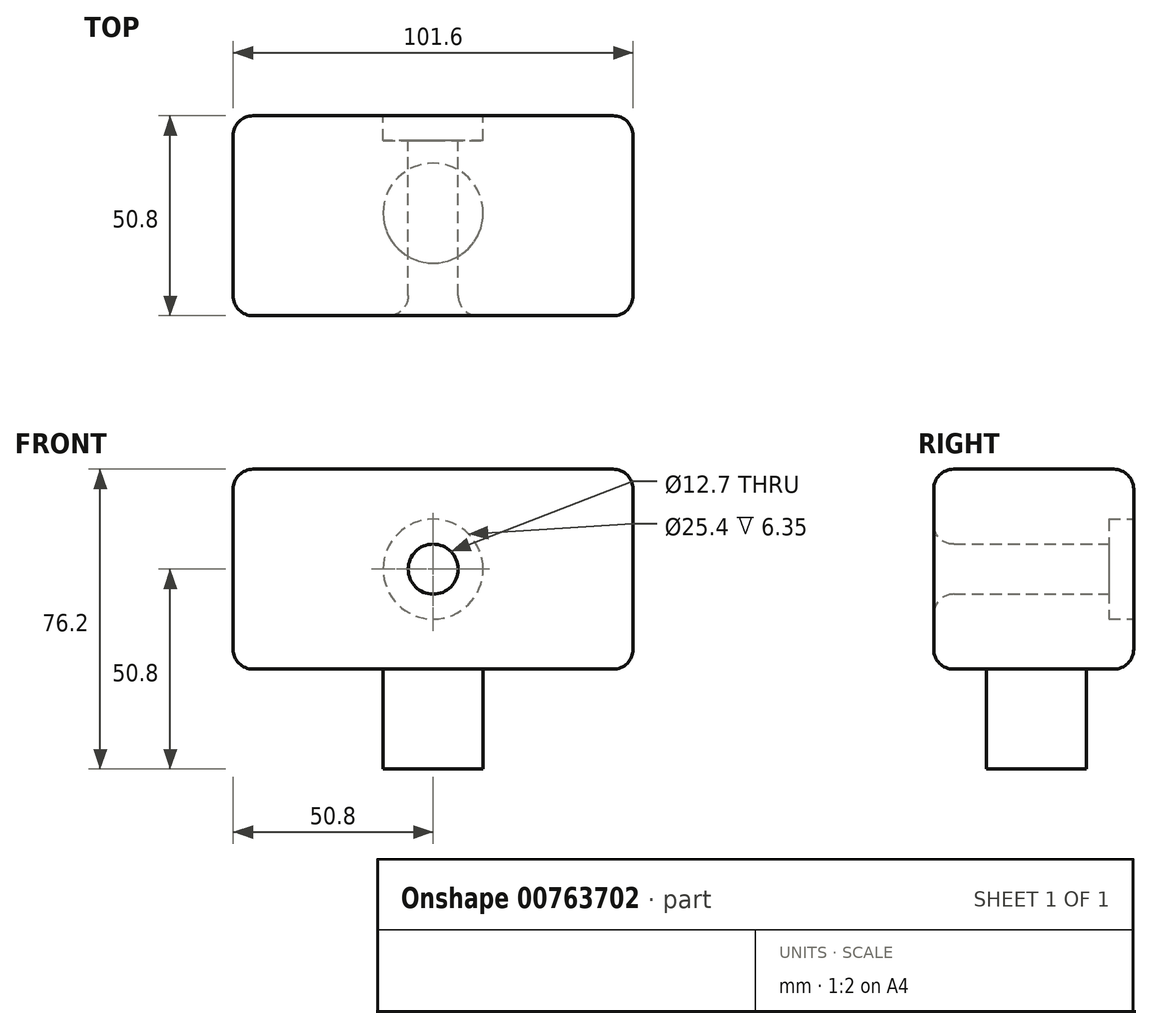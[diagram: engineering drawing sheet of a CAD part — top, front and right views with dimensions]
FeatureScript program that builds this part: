
annotation { "Feature Type Name" : "Feature", "Feature Type Description" : "" }
export const myFeature = defineFeature(function(context is Context, id is Id, definition is map)
    precondition{}
    {
        {
            var Q0;
            Q0=qCreatedBy(makeId("Top.planeOp"),FACE);
            var sketch = newSketch(context, id + "F0", { "sketchPlane" : qUnion([Q0])});
            skLineSegment(sketch, "E0.bottom", {"start": v(0, 0) * mm, "end": v(101.6, 0) * mm});
            skLineSegment(sketch, "E0.top", {"start": v(0, 50.8) * mm, "end": v(101.6, 50.8) * mm});
            skLineSegment(sketch, "E0.left", {"start": v(0, 0) * mm, "end": v(0, 50.8) * mm});
            skLineSegment(sketch, "E0.right", {"start": v(101.6, 0) * mm, "end": v(101.6, 50.8) * mm});
            skSolve(sketch);
        }
        {
            var Q0;
            Q0=makeQuery(id+"F0.imprint","IMPRINT",FACE,{"disambiguationData":[TD([[makeQuery(id+"F0.imprint","IMPRINT",EDGE,{"derivedFrom":sQuery(id+"F0.wireOp",EDGE,"E0.bottom")}),1.0]])]});
            extrude(context, id + "F1", {"entities" : qUnion([Q0]), "depth" : 50.8 * mm, "offsetDistance" : 25.4 * mm});
        }
        {
            var Q0;
            Q0=makeQuery(id+"F1.opExtrude","SWEPT_FACE",FACE,{"disambiguationData":[OSD([sQuery(id+"F0.wireOp",EDGE,"E0.top")])]});
            var sketch = newSketch(context, id + "F2", { "sketchPlane" : qUnion([Q0])});
            skPoint(sketch, "E1", {"position": v(-50.8, 25.4) * mm});
            skSolve(sketch);
        }
        {
            var Q0;
            Q0=sQuery(id+"F2.wireOp",VERTEX,"E1");
            var Q1;
            Q1=makeQuery(id+"F1.opExtrude","SWEPT_BODY",BODY,{"disambiguationData":[OSD([sQuery(id+"F0.wireOp",EDGE,"E0.bottom"),sQuery(id+"F0.wireOp",EDGE,"E0.top"),sQuery(id+"F0.wireOp",EDGE,"E0.left"),sQuery(id+"F0.wireOp",EDGE,"E0.right")])]});
            hole(context, id + "F3", {"style" : HoleStyle.C_BORE, "endStyle" : HoleEndStyle.THROUGH, "holeDiameter" : 12.7 * mm, "cBoreDiameter" : 25.4 * mm, "cBoreDepth" : 6.35 * mm, "majorDiameter" : 6.35 * mm, "isTappedThrough" : true, "tappedDepth" : 12.7 * mm, "tapClearance" : 3, "locations" : qUnion([Q0]), "scope" : qUnion([Q1])});
        }
        {
            var Q0;
            Q0=makeQuery(id+"F1.opExtrude","CAP_FACE",FACE,{"disambiguationData":[OSD([sQuery(id+"F0.wireOp",EDGE,"E0.bottom"),sQuery(id+"F0.wireOp",EDGE,"E0.top"),sQuery(id+"F0.wireOp",EDGE,"E0.left"),sQuery(id+"F0.wireOp",EDGE,"E0.right")])],"isStart":true});
            cPlane(context, id + "F4", {"entities" : qUnion([Q0]), "cplaneType" : CPlaneType.OFFSET, "offset" : 25.4 * mm, "width" : 152.4 * mm, "height" : 152.4 * mm});
        }
        {
            var Q0;
            Q0=qCreatedBy(id+"F4.planeOp",FACE);
            var sketch = newSketch(context, id + "F5", { "sketchPlane" : qUnion([Q0])});
            skCircle(sketch, "E2", {"center": v(50.8, -26.06) * mm, "radius": 12.7 * mm});
            skSolve(sketch);
        }
        {
            var Q0;
            Q0=makeQuery(id+"F5.imprint","IMPRINT",FACE,{"disambiguationData":[TD([[makeQuery(id+"F5.imprint","IMPRINT",EDGE,{"derivedFrom":sQuery(id+"F5.wireOp",EDGE,"E2")}),1.0]])]});
            extrude(context, id + "F6", {"entities" : qUnion([Q0]), "endBound" : BoundingType.UP_TO_NEXT, "oppositeDirection" : true, "depth" : 25.4 * mm, "offsetDistance" : 25.4 * mm});
        }
        {
            var Q0;
            Q0=makeQuery(id+"F1.opExtrude","SWEPT_FACE",FACE,{"disambiguationData":[OSD([sQuery(id+"F0.wireOp",EDGE,"E0.right")])]});
            var Q1;
            Q1=makeQuery(id+"F1.opExtrude","SWEPT_FACE",FACE,{"disambiguationData":[OSD([sQuery(id+"F0.wireOp",EDGE,"E0.left")])]});
            var Q2;
            Q2=makeQuery(id+"F1.opExtrude","CAP_FACE",FACE,{"disambiguationData":[OSD([sQuery(id+"F0.wireOp",EDGE,"E0.bottom"),sQuery(id+"F0.wireOp",EDGE,"E0.top"),sQuery(id+"F0.wireOp",EDGE,"E0.left"),sQuery(id+"F0.wireOp",EDGE,"E0.right")])],"isStart":false});
            var Q3;
            Q3=makeQuery(id+"F1.opExtrude","SWEPT_FACE",FACE,{"disambiguationData":[OSD([sQuery(id+"F0.wireOp",EDGE,"E0.bottom")])]});
            var Q4;
            Q4=makeQuery(id+"F1.opExtrude","CAP_FACE",FACE,{"disambiguationData":[OSD([sQuery(id+"F0.wireOp",EDGE,"E0.bottom"),sQuery(id+"F0.wireOp",EDGE,"E0.top"),sQuery(id+"F0.wireOp",EDGE,"E0.left"),sQuery(id+"F0.wireOp",EDGE,"E0.right")])],"isStart":true});
            fillet(context, id + "F7", {"entities" : qUnion([Q0, Q1, Q2, Q3, Q4]), "radius" : 5.08 * mm, "tangentPropagation" : true, "allowEdgeOverflow" : false});
        }
    });
